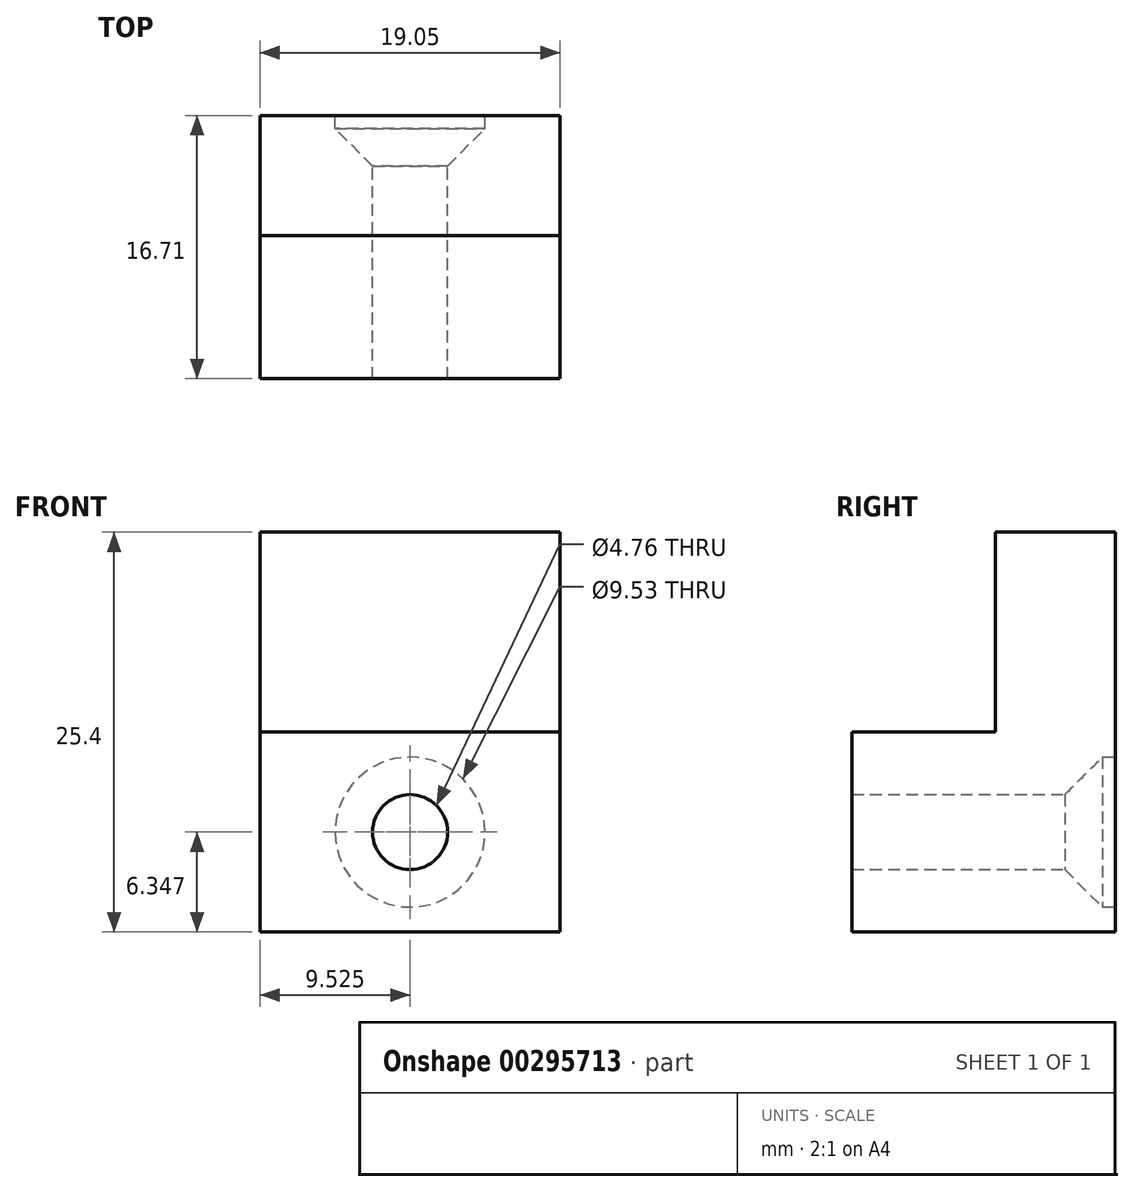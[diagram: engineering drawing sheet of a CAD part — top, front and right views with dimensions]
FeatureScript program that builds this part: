
annotation { "Feature Type Name" : "Feature", "Feature Type Description" : "" }
export const myFeature = defineFeature(function(context is Context, id is Id, definition is map)
    precondition{}
    {
        {
            var Q0;
            Q0=qCreatedBy(makeId("Right.planeOp"),FACE);
            var sketch = newSketch(context, id + "F0", { "sketchPlane" : qUnion([Q0])});
            skLineSegment(sketch, "E0", {"start": v(-12.21, -18.03) * mm, "end": v(-3.12, -18.03) * mm});
            skLineSegment(sketch, "E1", {"start": v(-3.12, -18.03) * mm, "end": v(-3.12, -5.33) * mm});
            skLineSegment(sketch, "E2", {"start": v(-3.12, -5.33) * mm, "end": v(4.5, -5.33) * mm});
            skLineSegment(sketch, "E3", {"start": v(4.5, -5.33) * mm, "end": v(4.5, -30.73) * mm});
            skLineSegment(sketch, "E4", {"start": v(4.5, -30.73) * mm, "end": v(-12.21, -30.73) * mm});
            skLineSegment(sketch, "E5", {"start": v(-12.21, -30.73) * mm, "end": v(-12.21, -18.03) * mm});
            skSolve(sketch);
        }
        {
            var Q0;
            Q0 = qSketchRegion(id + "F0", true);
            extrude(context, id + "F1", {"entities" : qUnion([Q0]), "depth" : 19.05 * mm});
        }
        {
            var Q0;
            Q0=makeQuery(id+"F1.opExtrude","SWEPT_FACE",FACE,{"disambiguationData":[OSD([sQuery(id+"F0.wireOp",EDGE,"E3")])]});
            cPlane(context, id + "F2", {"entities" : qUnion([Q0]), "cplaneType" : CPlaneType.OFFSET, "offset" : 0 * mm, "width" : 152.4 * mm, "height" : 152.4 * mm});
        }
        {
            var Q0;
            Q0=qCreatedBy(id+"F2.planeOp",FACE);
            var sketch = newSketch(context, id + "F3", { "sketchPlane" : qUnion([Q0])});
            skLineSegment(sketch, "E6.0.0", {"start": v(0, -18.03) * mm, "end": v(0, -30.73) * mm, "construction": true});
            skLineSegment(sketch, "E6.0.1", {"start": v(0, -30.73) * mm, "end": v(-19.05, -30.73) * mm, "construction": true});
            skLineSegment(sketch, "E6.0.2", {"start": v(-19.05, -30.73) * mm, "end": v(-19.05, -18.03) * mm, "construction": true});
            skLineSegment(sketch, "E6.0.3", {"start": v(-19.05, -18.03) * mm, "end": v(0, -18.03) * mm, "construction": true});
            skLineSegment(sketch, "E7.0.0", {"start": v(0, -5.33) * mm, "end": v(0, -18.03) * mm, "construction": true});
            skLineSegment(sketch, "E7.0.1", {"start": v(0, -18.03) * mm, "end": v(-19.05, -18.03) * mm, "construction": true});
            skLineSegment(sketch, "E7.0.2", {"start": v(-19.05, -18.03) * mm, "end": v(-19.05, -5.33) * mm, "construction": true});
            skLineSegment(sketch, "E7.0.3", {"start": v(-19.05, -5.33) * mm, "end": v(0, -5.33) * mm, "construction": true});
            skCircle(sketch, "E8", {"center": v(-9.53, -24.38) * mm, "radius": 2.38 * mm});
            skPoint(sketch, "E8.centerSnap0", {"position": v(-19.05, -24.38) * mm});
            skPoint(sketch, "E8.centerSnap1", {"position": v(-9.53, -18.03) * mm});
            skSolve(sketch);
        }
        {
            var Q0;
            Q0 = qSketchRegion(id + "F3", true);
            var Q1;
            Q1=makeQuery(id+"F1.opExtrude","SWEPT_FACE",FACE,{"disambiguationData":[OSD([sQuery(id+"F0.wireOp",EDGE,"E5")])]});
            extrude(context, id + "F4", {"entities" : qUnion([Q0]), "operationType" : NewBodyOperationType.REMOVE, "endBound" : BoundingType.UP_TO_SURFACE, "oppositeDirection" : true, "endBoundEntityFace" : qUnion([Q1]), "depth" : 25.4 * mm});
        }
        {
            var Q0;
            Q0=qCreatedBy(id+"F2.planeOp",FACE);
            var sketch = newSketch(context, id + "F5", { "sketchPlane" : qUnion([Q0])});
            skCircle(sketch, "E9.0", {"center": v(-9.53, -24.38) * mm, "radius": 2.38 * mm, "construction": true});
            skCircle(sketch, "E10", {"center": v(-9.53, -24.38) * mm, "radius": 4.76 * mm});
            skSolve(sketch);
        }
        {
            var Q0;
            Q0 = qSketchRegion(id + "F5", true);
            extrude(context, id + "F6", {"entities" : qUnion([Q0]), "operationType" : NewBodyOperationType.REMOVE, "oppositeDirection" : true, "depth" : 0.03 * mm});
        }
        {
            var Q0;
            Q0=makeQuery(id+"F6.boolean.opBoolean","INTERSECT",EDGE,{"derivedFrom":[makeQuery(id+"F4.boolean.opBoolean","COPY",FACE,{"derivedFrom":makeQuery(id+"F4.opExtrude","SWEPT_FACE",FACE,{"disambiguationData":[OSD([sQuery(id+"F3.wireOp",EDGE,"E8")])]})}),makeQuery(id+"F6.opExtrude","CAP_FACE",FACE,{"disambiguationData":[OSD([sQuery(id+"F5.wireOp",EDGE,"E10")])],"isStart":false})]});
            chamfer(context, id + "F7", {"entities" : qUnion([Q0]), "width" : 3.17 * mm, "tangentPropagation" : true});
        }
    });
